# Revit family: Hager-IC-IP30-sistema-NoHosted-ES-es
name_source: partatom
category: Electrical Equipment
units: mm (PartAtom-declared; Revit-internal decimal feet)

## family parameters
Always vertical = Yes
Cut with Voids When Loaded = No
Panel Configuration = Two Columns, Circuits Across
Part Type = Panelboard
Room Calculation Point = No
Round Connector Dimension = Use Diameter
Shared = No
Work Plane-Based = Yes

## types (11) — shared parameters
Default Elevation = 1219 mm
EF000007 - Color = EV000202 - Blanco
EF000116 - Número RAL = 9010
EF000118 - Con placa de montaje = No
EF001062 - Versión de EMC = No
EF001088 - Posibilidad de extensión = Yes
EF001131 - Profundidad interna = 72 mm  [stored 0.23622 ft]
EF001134 - Carril DIN = Yes
EF001596 - Material de la carcasa = EV000139 - Plástico
EF004462 - Tipo de cierre = EV000154 - Otros
EF005474 - Grado de protección (IP) = EV006410 - IP30
EF006244 - Tapa/puerta transparente = No
EF006306 - Con cierre = No
EF009212 - Versión de la cubierta = EV000116 - Cerrado
EF015776 - Borne de tierra = No
EF015777 - Borne neutro = No
EF015941 - Puerta de transmisión de señal = Yes
HG000001 - Número de columnas = 1
HG000003 - Gama = IC
HG000005 - Grosor = 3 mm  [stored 0.00984252 ft]
HG000009 - Puerta batiente doble = No
HG000010 - Puertas asimétricas = No
HG000011 - Filas vacías desde abajo = No
HG000017 - Distancia entre polos = 18 mm  [stored 0.0590551 ft]
Manufacturer = Hager
Type Comments = IC
zero-valued in all types: HG000007 - Número de columnas vacías, HG000008 - Número de filas vacías

## per-type parameters (varying)
| type | EF000003 - Tipo de montaje | EF000008 - Anchura | EF000040 - Altura | EF000049 - Profundidad | EF000218 - Profundidad de instalación | EF000266 - Número de filas | EF000332 - Altura de la instalación | EF000846 - Anchura de instalación | EF002950 - Anchura de unidades de división | HG000002 - Con puerta o tapa | HG000004 - Referencia del fabricante | HG000006 - Empotrado | Model |
| Montado empotrado IP30 A308 A351 P93 12 unidad de división - VR212NE | EV000383 - Montado empotrado (escayola) | 308 mm | 351 mm | 93 mm | 72 mm  [stored 0.23622 ft] | 2 | 333 mm | 290 mm | 12 | Yes | VR212NE | Yes | VR212NE |
| Montado empotrado IP30 A308 A351 P93 12 unidad de división - VR212NE1 | EV000383 - Montado empotrado (escayola) | 308 mm | 351 mm | 93 mm | 72 mm  [stored 0.23622 ft] | 2 | 333 mm | 290 mm | 12 | Yes | VR212NE1 | Yes | VR212NE1 |
| Montado empotrado IP30 A308 A351 P93 12 unidad de división - VR212NE2 | EV000383 - Montado empotrado (escayola) | 308 mm | 351 mm | 93 mm | 72 mm  [stored 0.23622 ft] | 2 | 333 mm | 290 mm | 12 | Yes | VR212NE2 | Yes | VR212NE2 |
| Montado empotrado IP30 A308 A351 P93 12 unidad de división - VR212NE3 | EV000383 - Montado empotrado (escayola) | 308 mm | 351 mm | 93 mm | 72 mm  [stored 0.23622 ft] | 2 | 333 mm | 290 mm | 12 | Yes | VR212NE3 | Yes | VR212NE3 |
| Montado empotrado IP30 A308 A351 P93 12 unidad de división - VR212NEB | EV000383 - Montado empotrado (escayola) | 308 mm | 351 mm | 93 mm | 72 mm  [stored 0.23622 ft] | 2 | 333 mm | 290 mm | 12 | Yes | VR212NEB | Yes | VR212NEB |
| Montado empotrado IP30 A308 A351 P93 12 unidad de división - VR212NH | EV000383 - Montado empotrado (escayola) | 308 mm | 351 mm | 93 mm | 72 mm  [stored 0.23622 ft] | 2 | 333 mm | 290 mm | 12 | Yes | VR212NH | Yes | VR212NH |
| Montado empotrado IP30 A308 A351 P93 12 unidad de división - VR212NH1 | EV000383 - Montado empotrado (escayola) | 308 mm | 351 mm | 93 mm | 72 mm  [stored 0.23622 ft] | 2 | 333 mm | 290 mm | 12 | Yes | VR212NH1 | Yes | VR212NH1 |
| Montado superficial IP30 A27.5 A163.5 P71 1 unidad de división - VD101NE | EV000384 - Montado superficial (escayola) | 28 mm | 164 mm  [stored 0.538058 ft] | 71 mm  [stored 0.23294 ft] | 0 mm  [stored 0 ft] | 1 | 0 mm  [stored 0 ft] | 0 mm  [stored 0 ft] | 1 | No | VD101NE | No | VD101NE |
| Montado superficial IP30 A45.5 A163.5 P71 2 unidad de división - VD102NE | EV000384 - Montado superficial (escayola) | 46 mm | 164 mm  [stored 0.538058 ft] | 71 mm  [stored 0.23294 ft] | 0 mm  [stored 0 ft] | 1 | 0 mm  [stored 0 ft] | 0 mm  [stored 0 ft] | 2 | No | VD102NE | No | VD102NE |
| Montado superficial IP30 A63.5 A163.5 P71 3 unidad de división - VD103NE | EV000384 - Montado superficial (escayola) | 64 mm | 164 mm  [stored 0.538058 ft] | 71 mm  [stored 0.23294 ft] | 0 mm  [stored 0 ft] | 1 | 0 mm  [stored 0 ft] | 0 mm  [stored 0 ft] | 3 | No | VD103NE | No | VD103NE |
| Montado superficial IP30 A81.5 A163.5 P71 4 unidad de división - VD104NE | EV000384 - Montado superficial (escayola) | 82 mm  [stored 0.269029 ft] | 164 mm  [stored 0.538058 ft] | 71 mm  [stored 0.23294 ft] | 0 mm  [stored 0 ft] | 1 | 0 mm  [stored 0 ft] | 0 mm  [stored 0 ft] | 4 | No | VD104NE | No | VD104NE |

note: [stored X ft] marks values corroborated as IEEE doubles in the binary element streams (Revit-internal decimal feet)

## geometry (parser evidence)
native form markers: Sweep x13
no freeform markers — native parametric forms only
